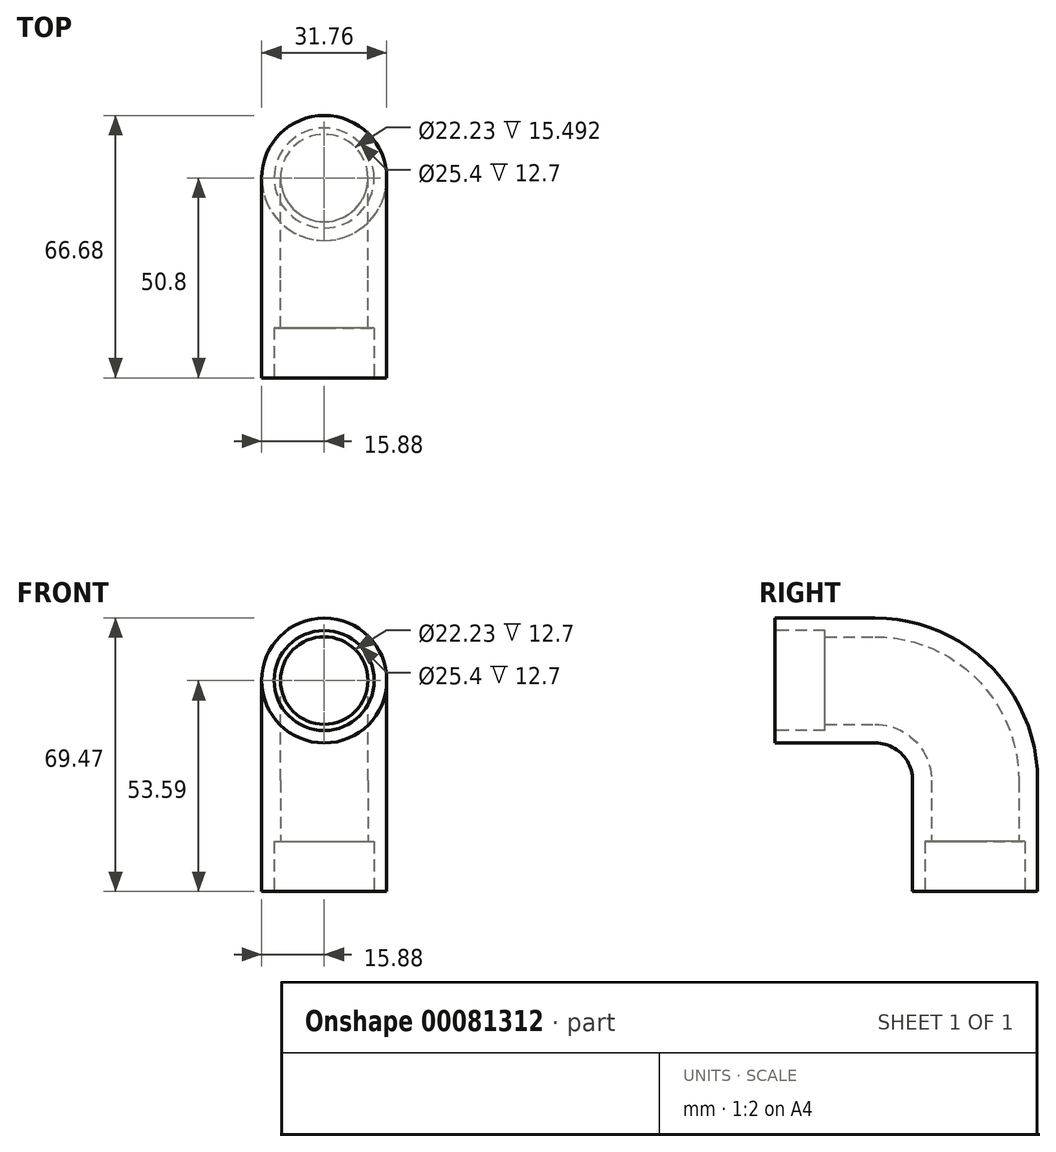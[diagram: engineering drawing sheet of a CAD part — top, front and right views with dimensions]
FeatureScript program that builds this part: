
annotation { "Feature Type Name" : "Feature", "Feature Type Description" : "" }
export const myFeature = defineFeature(function(context is Context, id is Id, definition is map)
    precondition{}
    {
        {
            var Q0;
            Q0=qCreatedBy(makeId("Front.planeOp"),FACE);
            var sketch = newSketch(context, id + "F0", { "sketchPlane" : qUnion([Q0])});
            skCircle(sketch, "E0", {"center": v(0, 0) * mm, "radius": 15.88 * mm});
            skCircle(sketch, "E1", {"center": v(0, 0) * mm, "radius": 11.11 * mm});
            skSolve(sketch);
        }
        {
            var Q0;
            Q0=qCreatedBy(makeId("Right.planeOp"),FACE);
            var sketch = newSketch(context, id + "F1", { "sketchPlane" : qUnion([Q0])});
            skLineSegment(sketch, "E2", {"start": v(0, 0) * mm, "end": v(25.4, 0) * mm});
            skLineSegment(sketch, "E3", {"start": v(25.4, 0) * mm, "end": v(25.4, 0) * mm});
            skLineSegment(sketch, "E4", {"start": v(50.8, -25.4) * mm, "end": v(50.8, -53.6) * mm});
            skPoint(sketch, "E5.visualSharp", {"position": v(50.8, 0) * mm});
            skArc(sketch, "E5.filletArc", {"start": v(50.8, -25.4) * mm, "mid": v(43.36, -7.44) * mm, "end": v(25.4, 0) * mm});
            skSolve(sketch);
        }
        {
            var Q0;
            Q0=makeQuery(id+"F0.imprint","IMPRINT",FACE,{"disambiguationData":[TD([[makeQuery(id+"F0.imprint","IMPRINT",EDGE,{"derivedFrom":sQuery(id+"F0.wireOp",EDGE,"E0")}),1.0]])]});
            var Q1;
            Q1=sQuery(id+"F1.wireOp",EDGE,"E2");
            var Q2;
            Q2=sQuery(id+"F1.wireOp",EDGE,"E5.filletArc");
            var Q3;
            Q3=sQuery(id+"F1.wireOp",EDGE,"E4");
            sweep(context, id + "F2", {"profiles" : qUnion([Q0]), "path" : qUnion([Q1, Q2, Q3])});
        }
        {
            var Q0;
            Q0=qCreatedBy(makeId("Front.planeOp"),FACE);
            var sketch = newSketch(context, id + "F3", { "sketchPlane" : qUnion([Q0])});
            skCircle(sketch, "E6", {"center": v(0, 0) * mm, "radius": 12.7 * mm});
            skSolve(sketch);
        }
        {
            var Q0;
            Q0 = qSketchRegion(id + "F3", true);
            extrude(context, id + "F4", {"entities" : qUnion([Q0]), "operationType" : NewBodyOperationType.REMOVE, "oppositeDirection" : true, "depth" : 12.7 * mm});
        }
        {
            var Q0;
            Q0=makeQuery(id+"F2.opSweep","CAP_FACE",FACE,{"disambiguationData":[OSD([sQuery(id+"F0.wireOp",EDGE,"E0"),sQuery(id+"F0.wireOp",EDGE,"E1"),sQuery(id+"F1.wireOp",VERTEX,"E4.end")])],"isStart":false});
            var sketch = newSketch(context, id + "F5", { "sketchPlane" : qUnion([Q0])});
            skCircle(sketch, "E7", {"center": v(0, -50.8) * mm, "radius": 12.7 * mm});
            skSolve(sketch);
        }
        {
            var Q0;
            Q0 = qSketchRegion(id + "F5", true);
            extrude(context, id + "F6", {"entities" : qUnion([Q0]), "operationType" : NewBodyOperationType.REMOVE, "oppositeDirection" : true, "depth" : 12.7 * mm});
        }
    });
